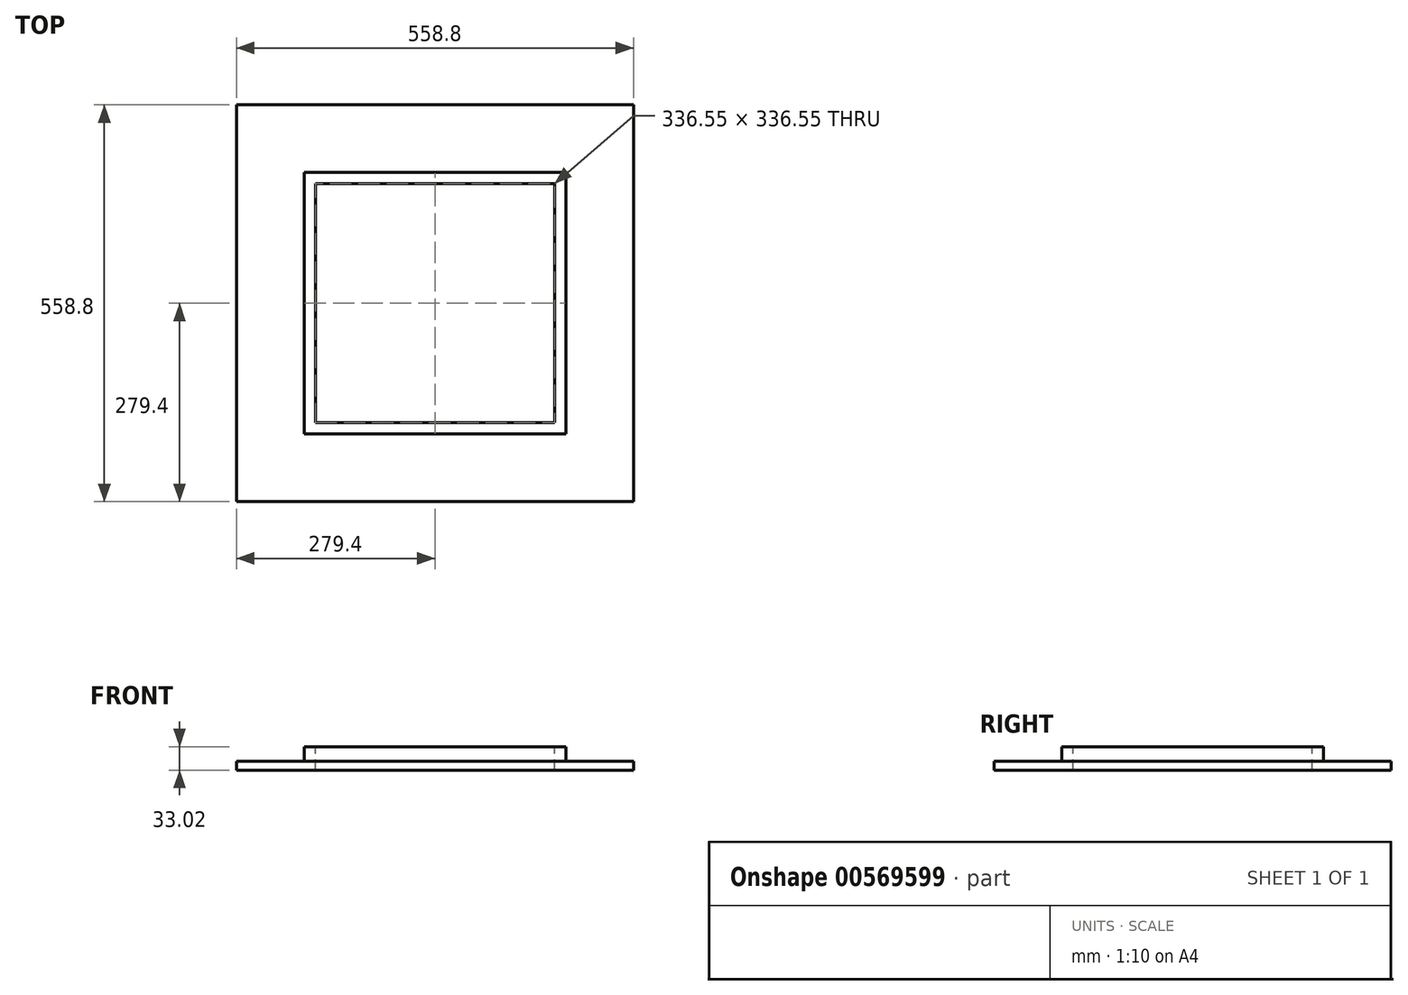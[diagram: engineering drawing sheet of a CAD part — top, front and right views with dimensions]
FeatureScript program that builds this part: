
annotation { "Feature Type Name" : "Feature", "Feature Type Description" : "" }
export const myFeature = defineFeature(function(context is Context, id is Id, definition is map)
    precondition{}
    {
        {
            var Q0;
            Q0=qCreatedBy(makeId("Top.planeOp"),FACE);
            var sketch = newSketch(context, id + "F0", { "sketchPlane" : qUnion([Q0])});
            skLineSegment(sketch, "E0.bottom", {"start": v(279.4, -279.4) * mm, "end": v(-279.4, -279.4) * mm});
            skLineSegment(sketch, "E0.top", {"start": v(279.4, 279.4) * mm, "end": v(-279.4, 279.4) * mm});
            skLineSegment(sketch, "E0.left", {"start": v(279.4, -279.4) * mm, "end": v(279.4, 279.4) * mm});
            skLineSegment(sketch, "E0.right", {"start": v(-279.4, -279.4) * mm, "end": v(-279.4, 279.4) * mm});
            skPoint(sketch, "E0.middle", {"position": v(0, 0) * mm});
            skSolve(sketch);
        }
        {
            var Q0;
            Q0 = qSketchRegion(id + "F0", true);
            extrude(context, id + "F1", {"entities" : qUnion([Q0]), "depth" : 12.7 * mm, "offsetDistance" : 25.4 * mm});
        }
        {
            var Q0;
            Q0=makeQuery(id+"F1.opExtrude","CAP_FACE",FACE,{"disambiguationData":[OSD([sQuery(id+"F0.wireOp",EDGE,"E0.bottom"),sQuery(id+"F0.wireOp",EDGE,"E0.top"),sQuery(id+"F0.wireOp",EDGE,"E0.left"),sQuery(id+"F0.wireOp",EDGE,"E0.right")])],"isStart":false});
            var sketch = newSketch(context, id + "F2", { "sketchPlane" : qUnion([Q0])});
            skLineSegment(sketch, "E1.bottom", {"start": v(184.15, -184.15) * mm, "end": v(-184.15, -184.15) * mm});
            skLineSegment(sketch, "E1.top", {"start": v(184.15, 184.15) * mm, "end": v(-184.15, 184.15) * mm});
            skLineSegment(sketch, "E1.left", {"start": v(184.15, -184.15) * mm, "end": v(184.15, 184.15) * mm});
            skLineSegment(sketch, "E1.right", {"start": v(-184.15, -184.15) * mm, "end": v(-184.15, 184.15) * mm});
            skPoint(sketch, "E1.middle", {"position": v(0, 0) * mm});
            skSolve(sketch);
        }
        {
            var Q0;
            Q0 = qSketchRegion(id + "F2", true);
            extrude(context, id + "F3", {"entities" : qUnion([Q0]), "operationType" : NewBodyOperationType.ADD, "depth" : 20.32 * mm, "offsetDistance" : 25.4 * mm});
        }
        {
            var Q0;
            Q0=makeQuery(id+"F3.opExtrude","CAP_FACE",FACE,{"disambiguationData":[OSD([sQuery(id+"F2.wireOp",EDGE,"E1.bottom"),sQuery(id+"F2.wireOp",EDGE,"E1.top"),sQuery(id+"F2.wireOp",EDGE,"E1.left"),sQuery(id+"F2.wireOp",EDGE,"E1.right")])],"isStart":false});
            var sketch = newSketch(context, id + "F4", { "sketchPlane" : qUnion([Q0])});
            skLineSegment(sketch, "E2.bottom", {"start": v(168.28, -168.27) * mm, "end": v(-168.28, -168.28) * mm});
            skLineSegment(sketch, "E2.top", {"start": v(168.28, 168.28) * mm, "end": v(-168.27, 168.27) * mm});
            skLineSegment(sketch, "E2.left", {"start": v(168.28, -168.27) * mm, "end": v(168.28, 168.27) * mm});
            skLineSegment(sketch, "E2.right", {"start": v(-168.28, -168.28) * mm, "end": v(-168.27, 168.28) * mm});
            skPoint(sketch, "E2.middle", {"position": v(0, 0) * mm});
            skSolve(sketch);
        }
        {
            var Q0;
            Q0 = qSketchRegion(id + "F4", true);
            extrude(context, id + "F5", {"entities" : qUnion([Q0]), "operationType" : NewBodyOperationType.REMOVE, "oppositeDirection" : true, "depth" : 121.92 * mm, "offsetDistance" : 25.4 * mm});
        }
    });
